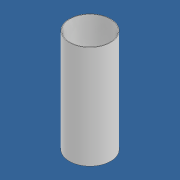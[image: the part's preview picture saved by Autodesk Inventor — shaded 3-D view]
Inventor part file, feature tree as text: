
AUTODESK INVENTOR PART (.ipt)
format: ipt  version: 2021 (Build 250183000, 183)  size: 78,848 bytes
history: native  units: in
note: dims shown in document units (in); Inventor stores cm internally (conversion verified against a paired STEP export)
features: extrude x1, sketch x1
ambient origin geometry x8: Origin, YZ Plane, XZ Plane, XY Plane, X Axis, Y Axis, Z Axis, Center Point
bodies: Solid1 (feature_tree)
feature tree (2):
  extrude  "Extrusion1"  Depth=10.0in
  sketch  "Sketch1"  dims[d0=4.0157in d1=3.9016in d2=10.0in d3=0.0in]
